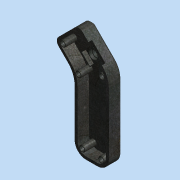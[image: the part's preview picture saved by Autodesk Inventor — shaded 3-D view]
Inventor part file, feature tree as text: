
AUTODESK INVENTOR PART (.ipt)
format: ipt  version: 2015 (Build 190159000, 159)  size: 280,576 bytes
history: native  units: in
note: dims shown in document units (in); Inventor stores cm internally (conversion verified against a paired STEP export)
features: extrude x8, sketch x6, projected_geometry x3, plane x2, shell x1, chamfer x1
ambient origin geometry x8: Origin, YZ Plane, XZ Plane, XY Plane, X Axis, Y Axis, Z Axis, Center Point
bodies: Solid1 (feature_tree), Solid2 (feature_tree)
feature tree (21):
  extrude  "Extrusion1"  Depth=1.5in
  shell  "Shell1"  Thickness=1.5in
  extrude  "Extrusion2"  Depth=1.25in
  sketch  "Sketch3"  dims[d5=1.0in d6=0.25in]
  extrude  "Extrusion3"  Depth=0.25in
  extrude  "Extrusion4"  Depth=0.625in TaperAngle=0.0deg
  sketch  "Sketch4"  dims[d7=0.5in d8=0.625in d9=0.0in]
  plane  "Work Plane1"
  extrude  "Extrusion5"  Depth=0.125in
  sketch  "Sketch5"  dims[d10=0.125in d11=0.75in]
  extrude  "Extrusion6"  Depth=0.5in TaperAngle=0.0deg
  extrude  "Extrusion7"  Depth=1.0in
  chamfer  "Chamfer1"  Distance=1.0625in
  sketch  "Sketch6"  dims[d12=0.1562in d13=0.5in d14=0.0in d15=1.0in d16=1.0625in d17=0.5in d18=0.0in d19=0.125in d20=0.0in d21=0.375in d23=0.0312in d24=0.0312in d25=0.0312in d26=0.0312in d27=-0.125in d28=0.125in d29=0.0in d30=0.2635in d31=0.201in d32=45.0deg d33=0.2635in d34=0.201in d35=0.2635in d36=0.201in d37=0.125in d38=0.0in d39=0.0in d40=0.0in d41=0.2635in d42=0.201in d45=0.125in d46=0.125in d47=45.0deg d48=0.25in d49=0.5in d50=-0.25in d51=0.125in d52=0.0in d53=0.0625in]
  plane  "Work Plane2"
  extrude  "Extrusion8"  Depth=0.5in TaperAngle=0.0deg
  sketch  "Sketch1"  dims[d0=45.0deg d1=1.5in d2=1.5in]
  sketch  "Sketch2"  dims[d3=3.0in d4=1.25in]
  projected_geometry  "Projected Loop1"
  projected_geometry  "Projected Loop2"
  projected_geometry  "Projected Loop3"
